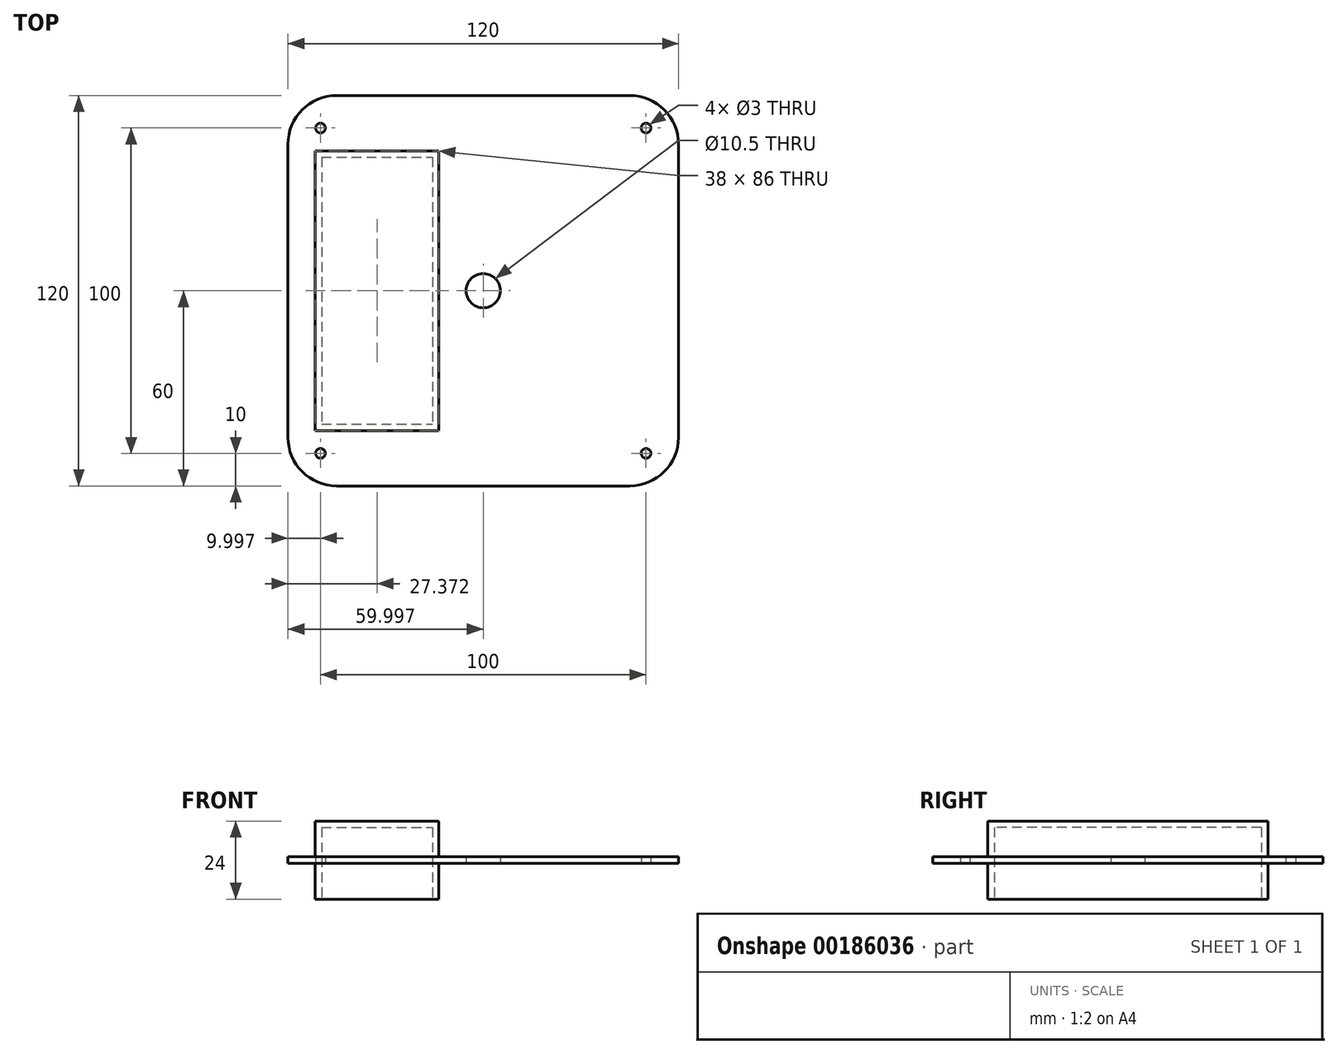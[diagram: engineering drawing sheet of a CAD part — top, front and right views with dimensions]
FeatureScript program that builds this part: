
annotation { "Feature Type Name" : "Feature", "Feature Type Description" : "" }
export const myFeature = defineFeature(function(context is Context, id is Id, definition is map)
    precondition{}
    {
        {
            assignVariable(context, id + "F0", {"name" : "driver_h", "anyValue" : 22});
        }
        {
            assignVariable(context, id + "F1", {"name" : "tykkelse", "anyValue" : 2});
        }
        {
            var Q0;
            Q0=qCreatedBy(makeId("Top.planeOp"),FACE);
            var sketch = newSketch(context, id + "F2", { "sketchPlane" : qUnion([Q0])});
            skLineSegment(sketch, "E0.bottom", {"start": v(-4.87, 8.8) * mm, "end": v(-94.87, 8.8) * mm});
            skLineSegment(sketch, "E0.top", {"start": v(-4.87, 128.8) * mm, "end": v(-94.87, 128.8) * mm});
            skLineSegment(sketch, "E0.left", {"start": v(10.13, 23.8) * mm, "end": v(10.13, 113.8) * mm});
            skLineSegment(sketch, "E0.right", {"start": v(-109.87, 23.8) * mm, "end": v(-109.87, 113.8) * mm});
            skLineSegment(sketch, "E1", {"start": v(-49.87, 128.8) * mm, "end": v(-49.87, 8.8) * mm, "construction": true});
            skCircle(sketch, "E2", {"center": v(-49.87, 68.8) * mm, "radius": 5.25 * mm});
            skLineSegment(sketch, "E3.bottom", {"start": v(-99.5, 109.8) * mm, "end": v(-65.5, 109.8) * mm});
            skLineSegment(sketch, "E3.top", {"start": v(-99.5, 27.8) * mm, "end": v(-65.5, 27.8) * mm});
            skLineSegment(sketch, "E3.left", {"start": v(-99.5, 109.8) * mm, "end": v(-99.5, 27.8) * mm});
            skLineSegment(sketch, "E3.right", {"start": v(-65.5, 109.8) * mm, "end": v(-65.5, 27.8) * mm});
            skLineSegment(sketch, "E4.0", {"start": v(-101.5, 111.8) * mm, "end": v(-101.5, 25.8) * mm});
            skLineSegment(sketch, "E4.1", {"start": v(-101.5, 111.8) * mm, "end": v(-63.5, 111.8) * mm});
            skLineSegment(sketch, "E4.2", {"start": v(-63.5, 111.8) * mm, "end": v(-63.5, 25.8) * mm});
            skLineSegment(sketch, "E4.3", {"start": v(-101.5, 25.8) * mm, "end": v(-63.5, 25.8) * mm});
            skLineSegment(sketch, "E5", {"start": v(-82.5, 109.8) * mm, "end": v(-82.5, 27.8) * mm, "construction": true});
            skLineSegment(sketch, "E6", {"start": v(-82.5, 68.8) * mm, "end": v(-82.23, 68.8) * mm, "construction": true});
            skLineSegment(sketch, "E7", {"start": v(-109.87, 68.8) * mm, "end": v(-55.12, 68.8) * mm, "construction": true});
            skPoint(sketch, "E7.endSnap0", {"position": v(-63.5, 68.8) * mm});
            skPoint(sketch, "E8.visualSharp", {"position": v(-109.87, 128.8) * mm});
            skArc(sketch, "E8.filletArc", {"start": v(-94.87, 128.8) * mm, "mid": v(-105.48, 124.4) * mm, "end": v(-109.87, 113.8) * mm});
            skPoint(sketch, "E9.visualSharp", {"position": v(10.13, 128.8) * mm});
            skArc(sketch, "E9.filletArc", {"start": v(10.13, 113.8) * mm, "mid": v(5.73, 124.4) * mm, "end": v(-4.87, 128.8) * mm});
            skPoint(sketch, "E10.visualSharp", {"position": v(10.13, 8.8) * mm});
            skArc(sketch, "E10.filletArc", {"start": v(-4.87, 8.8) * mm, "mid": v(5.73, 13.2) * mm, "end": v(10.13, 23.8) * mm});
            skPoint(sketch, "E11.visualSharp", {"position": v(-109.87, 8.8) * mm});
            skArc(sketch, "E11.filletArc", {"start": v(-109.87, 23.8) * mm, "mid": v(-105.48, 13.2) * mm, "end": v(-94.87, 8.8) * mm});
            skCircle(sketch, "E12", {"center": v(-99.87, 118.8) * mm, "radius": 1.5 * mm});
            skCircle(sketch, "E13.0.1.0", {"center": v(-99.87, 18.8) * mm, "radius": 1.5 * mm});
            skCircle(sketch, "E13.1.0.0", {"center": v(0.13, 118.8) * mm, "radius": 1.5 * mm});
            skCircle(sketch, "E13.1.1.0", {"center": v(0.13, 18.8) * mm, "radius": 1.5 * mm});
            skCircle(sketch, "E13.2.0.0", {"center": v(100.13, 118.8) * mm, "radius": 1.5 * mm});
            skCircle(sketch, "E13.2.1.0", {"center": v(100.13, 18.8) * mm, "radius": 1.5 * mm});
            skLineSegment(sketch, "E13.direction1", {"start": v(-99.87, 118.8) * mm, "end": v(0.13, 118.8) * mm, "construction": true});
            skLineSegment(sketch, "E13.direction2", {"start": v(-99.87, 118.8) * mm, "end": v(-99.87, 18.8) * mm, "construction": true});
            skSolve(sketch);
        }
        {
            var Q0;
            Q0=makeQuery(id+"F2.imprint","IMPRINT",FACE,{"disambiguationData":[TD([[makeQuery(id+"F2.imprint","IMPRINT",EDGE,{"derivedFrom":sQuery(id+"F2.wireOp",EDGE,"E3.bottom")}),-1.0]])]});
            var Q1;
            Q1=makeQuery(id+"F2.imprint","IMPRINT",FACE,{"disambiguationData":[TD([[makeQuery(id+"F2.imprint","IMPRINT",EDGE,{"derivedFrom":sQuery(id+"F2.wireOp",EDGE,"E3.bottom")}),1.0]])]});
            extrude(context, id + "F3", {"entities" : qUnion([Q0, Q1]), "depth" : (getVariable(context, 'driver_h') / 2 + getVariable(context, 'tykkelse')) * mm});
        }
        {
            var Q0;
            Q0=makeQuery(id+"F2.imprint","IMPRINT",FACE,{"disambiguationData":[TD([[makeQuery(id+"F2.imprint","IMPRINT",EDGE,{"derivedFrom":sQuery(id+"F2.wireOp",EDGE,"E3.bottom")}),-1.0]])]});
            extrude(context, id + "F4", {"entities" : qUnion([Q0]), "operationType" : NewBodyOperationType.REMOVE, "depth" : (getVariable(context, 'driver_h') / 2) * mm});
        }
        {
            var Q0;
            Q0=makeQuery(id+"F2.imprint","IMPRINT",FACE,{"disambiguationData":[TD([[makeQuery(id+"F2.imprint","IMPRINT",EDGE,{"derivedFrom":sQuery(id+"F2.wireOp",EDGE,"E3.bottom")}),1.0]])]});
            extrude(context, id + "F5", {"entities" : qUnion([Q0]), "operationType" : NewBodyOperationType.ADD, "oppositeDirection" : true, "depth" : (getVariable(context, 'driver_h') / 2) * mm});
        }
        {
            var Q0;
            Q0=makeQuery(id+"F2.imprint","IMPRINT",FACE,{"disambiguationData":[TD([[makeQuery(id+"F2.imprint","IMPRINT",EDGE,{"derivedFrom":sQuery(id+"F2.wireOp",EDGE,"E0.bottom")}),-1.0]])]});
            extrude(context, id + "F6", {"entities" : qUnion([Q0]), "operationType" : NewBodyOperationType.ADD, "depth" : (getVariable(context, 'tykkelse')) * mm});
        }
    });
